# Revit family: NLRS_57_AIR_UN_round-vandal-resistand-wall-grill-wtrp_LT_sacs
name_source: partatom
category: Air Terminals
units: mm (PartAtom-declared; Revit-internal decimal feet)

## family parameters
Always vertical = Yes
Cut with Voids When Loaded = No
Part Type = Normal
Room Calculation Point = No
Round Connector Dimension = Use Diameter
Shared = No
Work Plane-Based = No

## types (2) — shared parameters
Assembly Code = 57.00
Default Elevation = 2400 mm
Description = Vandal resistant supply grill WTRP
Manufacturer = Solid Air Climate Solutions
Min Flow = 54.0 m³/h
Model = WTRP_S
NLRS_C_content_datum_uitgifte = 11-09-2025
NLRS_C_content_provider = Solid Air Climate Solutions
NLRS_C_content_versie = 4.22.00
NLRS_C_description = Vandal resistant supply grill WTRP
SACS_Data_Hidden = WTRP_S
SACS_Type_Selector_1 = W_RP_Grill : RAL 9010-55
SACS_Type_Selector_2 = W_RP_Grill : RAL 9016-30
SACS_Type_Selector_3 = W_RP_Grill : RAL 9016-70
SACS_Type_Selector_4 = W_RP_Grill : Custom

## per-type parameters (varying)
| type | Max Flow | SACS_Base_Index | SACS_Diameter | SACS_Factor_LpF1 | SACS_Factor_LpF2 | SACS_Factor_PsF1 | SACS_Factor_PsF2 | SACS_Factor_WF1 | SACS_Factor_WF2 |
| 160 | 108.0 m³/h | 0 | 160 mm  [stored 0.524934 ft] | -104.332506 | 28.228583 | 0.004739 | 1.991276 | 0.068199 | 0.966973 |
| 200 | 216.0 m³/h | 1 | 200 mm  [stored 0.656168 ft] | -125.204151 | 29.96099 | 0.001474 | 2.020755 | 0.053619 | 0.91849 |

note: [stored X ft] marks values corroborated as IEEE doubles in the binary element streams (Revit-internal decimal feet)

## geometry (parser evidence)
native form markers: Sweep x12
no freeform markers — native parametric forms only
